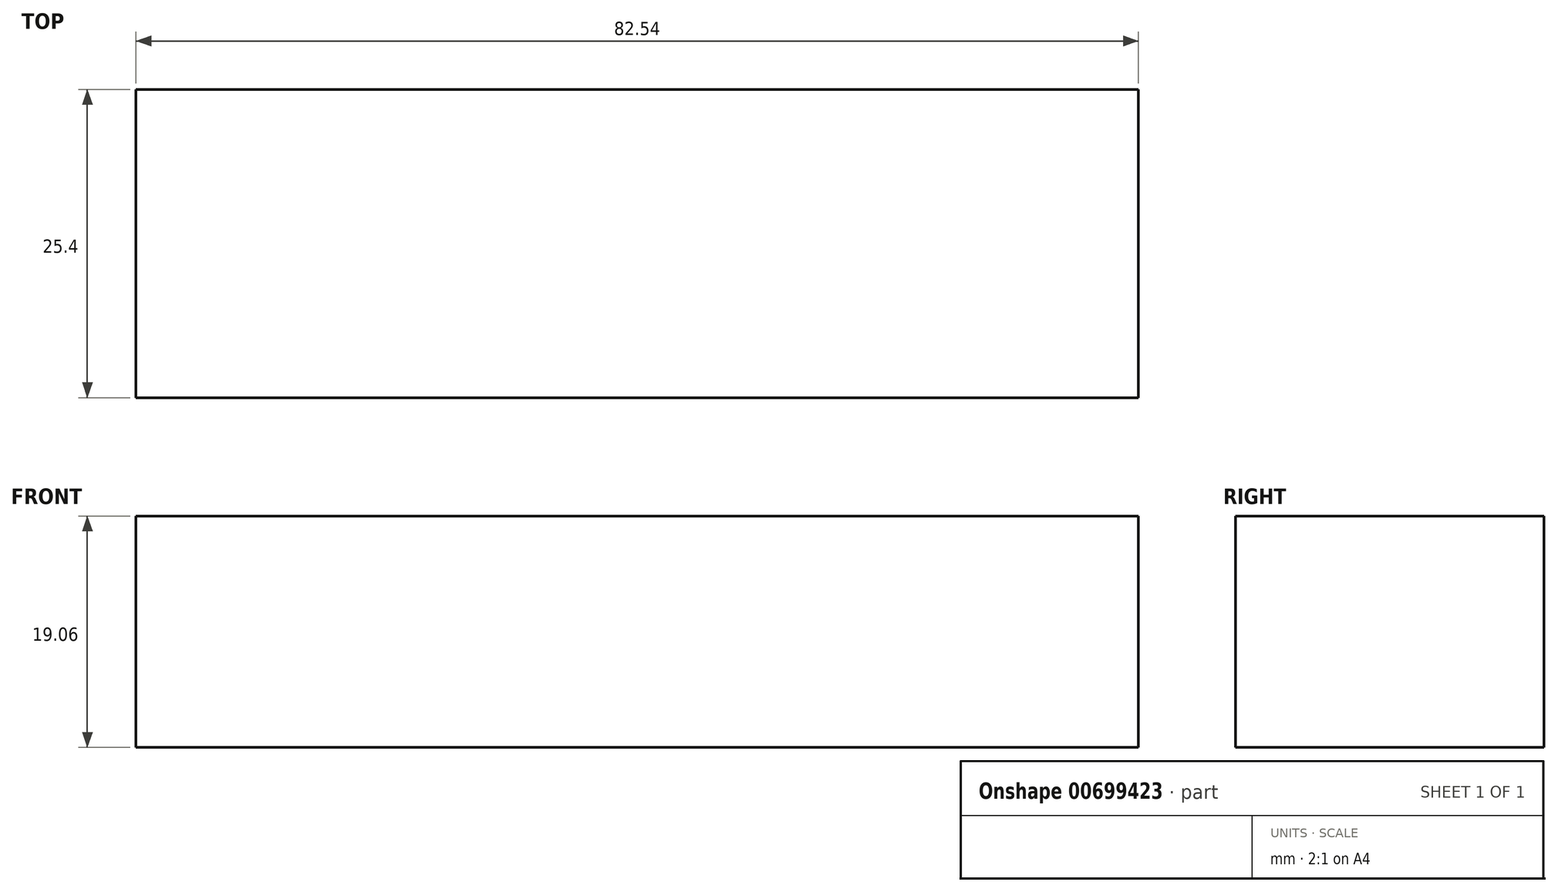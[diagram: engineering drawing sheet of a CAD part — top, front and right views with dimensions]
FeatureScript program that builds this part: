
annotation { "Feature Type Name" : "Feature", "Feature Type Description" : "" }
export const myFeature = defineFeature(function(context is Context, id is Id, definition is map)
    precondition{}
    {
        {
            var Q0;
            Q0=qCreatedBy(makeId("Front.planeOp"),FACE);
            var sketch = newSketch(context, id + "F0", { "sketchPlane" : qUnion([Q0])});
            skLineSegment(sketch, "E0.bottom", {"start": v(-41.28, 9.52) * mm, "end": v(41.27, 9.53) * mm});
            skLineSegment(sketch, "E0.top", {"start": v(-41.28, -9.53) * mm, "end": v(41.28, -9.53) * mm});
            skLineSegment(sketch, "E0.left", {"start": v(-41.28, 9.52) * mm, "end": v(-41.27, -9.53) * mm});
            skLineSegment(sketch, "E0.right", {"start": v(41.28, 9.53) * mm, "end": v(41.28, -9.52) * mm});
            skPoint(sketch, "E0.middle", {"position": v(0, 0) * mm});
            skLineSegment(sketch, "E1.bottom", {"start": v(72.98, 38.3) * mm, "end": v(123.78, 38.3) * mm});
            skLineSegment(sketch, "E1.top", {"start": v(72.98, 66.87) * mm, "end": v(123.78, 66.87) * mm});
            skLineSegment(sketch, "E1.left", {"start": v(72.98, 38.3) * mm, "end": v(72.98, 66.87) * mm});
            skLineSegment(sketch, "E1.right", {"start": v(123.78, 38.3) * mm, "end": v(123.78, 66.87) * mm});
            skPoint(sketch, "E1.middle", {"position": v(98.38, 52.58) * mm});
            skLineSegment(sketch, "E2", {"start": v(41.27, 9.53) * mm, "end": v(41.27, 37.56) * mm});
            skArc(sketch, "E3", {"start": v(41.27, 37.56) * mm, "mid": v(46.83, 49.63) * mm, "end": v(59.6, 53.25) * mm});
            skLineSegment(sketch, "E4", {"start": v(59.6, 53.25) * mm, "end": v(92.99, 53.25) * mm});
            skSolve(sketch);
        }
        {
            var Q0;
            Q0=makeQuery(id+"F0.imprint","IMPRINT",FACE,{"disambiguationData":[TD([[makeQuery(id+"F0.imprint","IMPRINT",EDGE,{"derivedFrom":sQuery(id+"F0.wireOp",EDGE,"E0.bottom")}),-1.0]])]});
            extrude(context, id + "F1", {"entities" : qUnion([Q0]), "depth" : 25.4 * mm, "offsetDistance" : 25.4 * mm});
        }
    });
